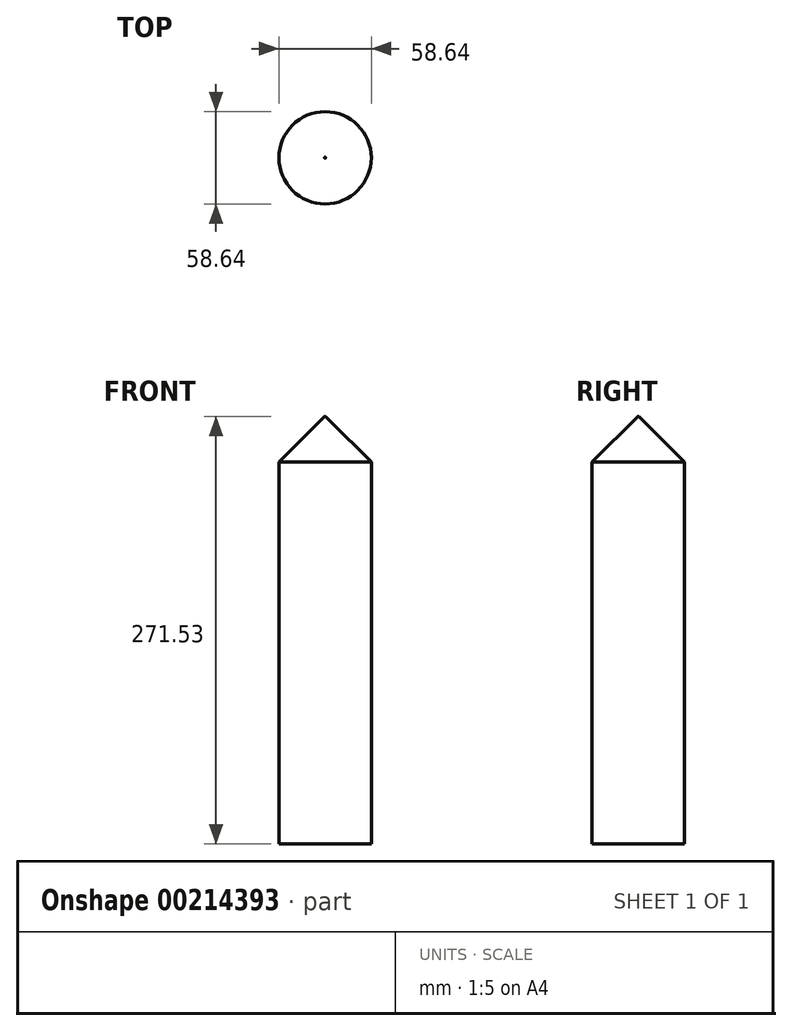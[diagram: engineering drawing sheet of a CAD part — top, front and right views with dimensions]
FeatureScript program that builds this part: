
annotation { "Feature Type Name" : "Feature", "Feature Type Description" : "" }
export const myFeature = defineFeature(function(context is Context, id is Id, definition is map)
    precondition{}
    {
        {
            var Q0;
            Q0=qCreatedBy(makeId("Top.planeOp"),FACE);
            var sketch = newSketch(context, id + "F0", { "sketchPlane" : qUnion([Q0])});
            skCircle(sketch, "E0", {"center": v(0, 0) * mm, "radius": 29.32 * mm});
            skSolve(sketch);
        }
        {
            var Q0;
            Q0=makeQuery(id+"F0.imprint","IMPRINT",FACE,{"disambiguationData":[TD([[makeQuery(id+"F0.imprint","IMPRINT",EDGE,{"derivedFrom":sQuery(id+"F0.wireOp",EDGE,"E0")}),1.0]])]});
            extrude(context, id + "F1", {"entities" : qUnion([Q0]), "depth" : 68.33 * mm});
        }
        {
            var Q0;
            Q0=makeQuery(id+"F1.opExtrude","CAP_FACE",FACE,{"disambiguationData":[OSD([sQuery(id+"F0.wireOp",EDGE,"E0")])],"isStart":false});
            extrude(context, id + "F2", {"entities" : qUnion([Q0]), "operationType" : NewBodyOperationType.ADD, "depth" : 203.2 * mm, "hasDraft" : true, "draftAngle" : 0 * degree});
        }
        {
            var Q0;
            Q0=makeQuery(id+"F2.opExtrude","CAP_FACE",FACE,{"disambiguationData":[OSD([sQuery(id+"F0.wireOp",EDGE,"E0")])],"isStart":false});
            chamfer(context, id + "F3", {"entities" : qUnion([Q0]), "width" : 28.96 * mm, "tangentPropagation" : true});
        }
    });
